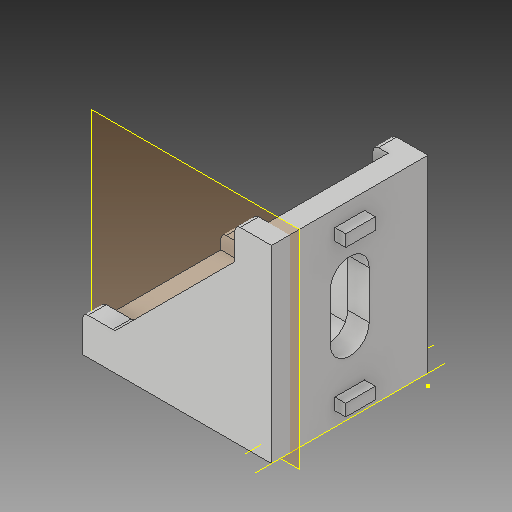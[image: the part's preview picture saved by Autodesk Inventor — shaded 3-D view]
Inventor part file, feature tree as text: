
AUTODESK INVENTOR PART (.ipt)
format: ipt  version: 2018 (Build 220112000, 112)  size: 186,368 bytes
history: native  units: mm
features: sketch x8, other x5, plane x1
ambient origin geometry x8: Origin, YZ Plane, XZ Plane, XY Plane, X Axis, Y Axis, Z Axis, Center Point
bodies: Solid1 (feature_tree)
feature tree (14):
  other  "30mm Bracket_CPY_MIR2.ipt"
  other  "Solid1::30mm Bracket_CPY_MIR2.ipt"
  other  "TaggingFeature1"
  sketch  "Sketch1"  dims[d0=10.0mm]
  sketch  "Sketch2"
  sketch  "Sketch3"
  sketch  "Sketch4"
  sketch  "Sketch5"
  sketch  "Sketch7"
  sketch  "Sketch9"
  sketch  "Sketch10"
  plane  "Work Plane1"
  other  "Work Axis1"
  other  "Work Axis2"
